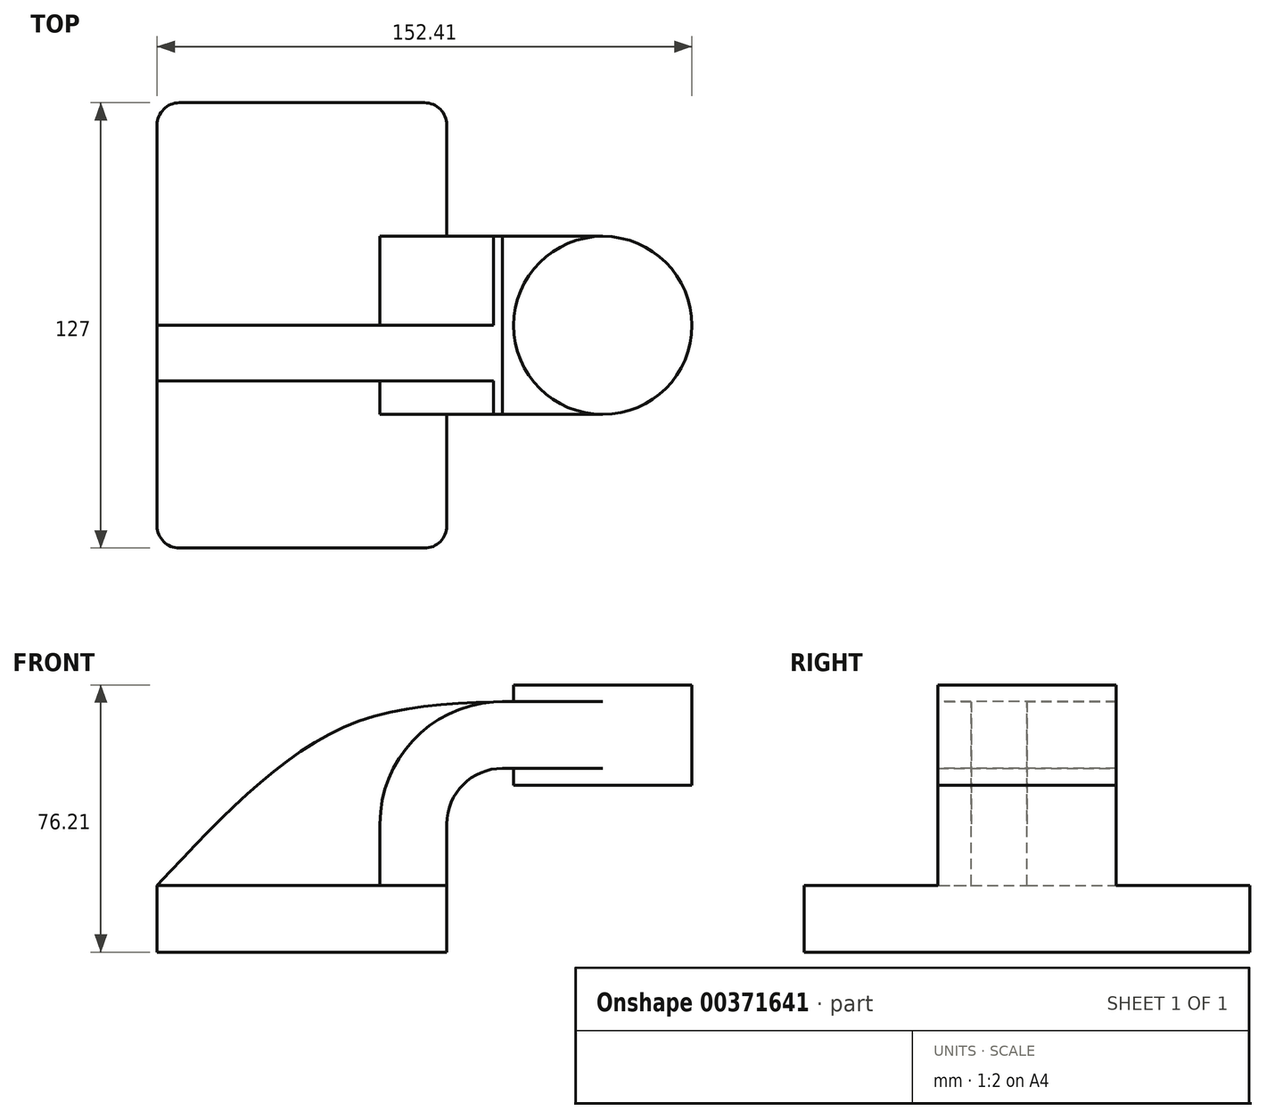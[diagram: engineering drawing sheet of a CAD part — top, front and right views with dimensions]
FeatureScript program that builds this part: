
annotation { "Feature Type Name" : "Feature", "Feature Type Description" : "" }
export const myFeature = defineFeature(function(context is Context, id is Id, definition is map)
    precondition{}
    {
        {
            var Q0;
            Q0=qCreatedBy(makeId("Front.planeOp"),FACE);
            var sketch = newSketch(context, id + "F0", { "sketchPlane" : qUnion([Q0])});
            skLineSegment(sketch, "E0.bottom", {"start": v(41.28, 9.52) * mm, "end": v(-41.28, 9.52) * mm});
            skLineSegment(sketch, "E0.top", {"start": v(41.28, -9.53) * mm, "end": v(-41.28, -9.53) * mm});
            skLineSegment(sketch, "E0.left", {"start": v(41.28, 9.53) * mm, "end": v(41.28, -9.53) * mm});
            skLineSegment(sketch, "E0.right", {"start": v(-41.28, 9.52) * mm, "end": v(-41.27, -9.53) * mm});
            skPoint(sketch, "E0.middle", {"position": v(0, 0) * mm});
            skLineSegment(sketch, "E1", {"start": v(41.28, 9.52) * mm, "end": v(41.28, 27) * mm});
            skArc(sketch, "E2", {"start": v(41.27, 27) * mm, "mid": v(45.92, 38.23) * mm, "end": v(57.15, 42.88) * mm});
            skLineSegment(sketch, "E3", {"start": v(57.15, 42.88) * mm, "end": v(85.73, 42.88) * mm});
            skLineSegment(sketch, "E4.bottom", {"start": v(60.33, 66.68) * mm, "end": v(111.13, 66.68) * mm});
            skLineSegment(sketch, "E4.top", {"start": v(60.33, 38.1) * mm, "end": v(111.13, 38.1) * mm});
            skLineSegment(sketch, "E4.left", {"start": v(60.33, 66.68) * mm, "end": v(60.33, 38.1) * mm});
            skLineSegment(sketch, "E4.right", {"start": v(111.13, 66.68) * mm, "end": v(111.13, 38.1) * mm});
            skPoint(sketch, "E4.middle", {"position": v(85.73, 52.39) * mm});
            skLineSegment(sketch, "E5.0", {"start": v(57.15, 61.93) * mm, "end": v(85.73, 61.93) * mm});
            skArc(sketch, "E5.1", {"start": v(22.23, 27) * mm, "mid": v(32.45, 51.7) * mm, "end": v(57.15, 61.93) * mm});
            skLineSegment(sketch, "E5.2", {"start": v(22.23, 9.52) * mm, "end": v(22.23, 27) * mm});
            skPoint(sketch, "E6.startSnap0", {"position": v(85.73, 66.68) * mm});
            skFitSpline(sketch, "E7", {"points": [v(-41.28, 9.52) * mm, v(-10.95, 39.6) * mm, v(19.24, 57.36) * mm, v(57.15, 61.93) * mm], "startDerivative": vector(85.37, 91.2) * mm, "endDerivative": vector(119, 4.27) * mm});
            skLineSegment(sketch, "E8", {"start": v(85.73, 66.68) * mm, "end": v(85.73, 38.1) * mm});
            skSolve(sketch);
        }
        {
            var Q0;
            Q0=makeQuery(id+"F0.imprint","IMPRINT",FACE,{"disambiguationData":[TD([[makeQuery(id+"F0.imprint","IMPRINT",EDGE,{"derivedFrom":sQuery(id+"F0.wireOp",EDGE,"E0.top")}),-1.0]])]});
            extrude(context, id + "F1", {"entities" : qUnion([Q0]), "endBound" : BoundingType.SYMMETRIC, "depth" : 127 * mm});
        }
        {
            var Q0;
            {var subQ8=sQuery(id+"F0.wireOp",EDGE,"E1");Q0=makeQuery(id+"F0.imprint","IMPRINT",FACE,{"disambiguationData":[TD([[makeQuery(id+"F0.imprint","IMPRINT",EDGE,{"derivedFrom":subQ8}),1.0]])]});}
            var Q1;
            {var subQ0=sQuery(id+"F0.wireOp",EDGE,"RDqRDKUh-tZSh-ccH2-2HAj-dexB6HYa6Owt");Q1=makeQuery(id+"F0.imprint","IMPRINT",FACE,{"disambiguationData":[TD([[makeQuery(id+"F0.imprint","IMPRINT",EDGE,{"derivedFrom":subQ0}),-1.0]])]});}
            var Q2;
            {var subQ0=sQuery(id+"F0.wireOp",EDGE,"E8");var subQ1=sQuery(id+"F0.wireOp",EDGE,"E3");var subQ2=makeQuery(id+"F0.imprint","INTERSECT",VERTEX,{"derivedFrom":[subQ1,subQ0]});Q2=makeQuery(id+"F0.imprint","IMPRINT",FACE,{"disambiguationData":[TD([[makeQuery(id+"F0.imprint","IMPRINT",EDGE,{"disambiguationData":[TD([[subQ2,1.0]])],"derivedFrom":subQ1}),1.0]])]});}
            extrude(context, id + "F2", {"entities" : qUnion([Q0, Q1, Q2]), "operationType" : NewBodyOperationType.ADD, "endBound" : BoundingType.SYMMETRIC, "depth" : 50.8 * mm});
        }
        {
            var Q0;
            {var subQ3=sQuery(id+"F0.wireOp",EDGE,"E5.2");Q0=makeQuery(id+"F0.imprint","IMPRINT",FACE,{"disambiguationData":[TD([[makeQuery(id+"F0.imprint","IMPRINT",EDGE,{"derivedFrom":subQ3}),1.0]])]});}
            extrude(context, id + "F3", {"entities" : qUnion([Q0]), "operationType" : NewBodyOperationType.ADD, "depth" : 15.88 * mm});
        }
        {
            var Q0;
            {var subQ4=sQuery(id+"F0.wireOp",EDGE,"E4.right");Q0=makeQuery(id+"F0.imprint","IMPRINT",FACE,{"disambiguationData":[TD([[makeQuery(id+"F0.imprint","IMPRINT",EDGE,{"derivedFrom":subQ4}),-1.0]])]});}
            var Q1;
            Q1=sQuery(id+"F0.wireOp",EDGE,"E8");
            revolve(context, id + "F4", {"operationType" : NewBodyOperationType.ADD, "entities" : qUnion([Q0]), "axis" : qUnion([Q1]), "revolveType" : RevolveType.FULL});
        }
        {
            var Q0;
            Q0=makeQuery(id+"F1.opExtrude","CAP_EDGE",EDGE,{"disambiguationData":[OSD([sQuery(id+"F0.wireOp",EDGE,"E0.right")])],"isStart":false});
            var Q1;
            Q1=makeQuery(id+"F1.opExtrude","CAP_EDGE",EDGE,{"disambiguationData":[OSD([sQuery(id+"F0.wireOp",EDGE,"E0.right")])],"isStart":true});
            var Q2;
            Q2=makeQuery(id+"F1.opExtrude","CAP_EDGE",EDGE,{"disambiguationData":[OSD([sQuery(id+"F0.wireOp",EDGE,"E0.left")])],"isStart":true});
            var Q3;
            Q3=makeQuery(id+"F1.opExtrude","CAP_EDGE",EDGE,{"disambiguationData":[OSD([sQuery(id+"F0.wireOp",EDGE,"E0.left")])],"isStart":false});
            fillet(context, id + "F5", {"entities" : qUnion([Q0, Q1, Q2, Q3]), "radius" : 6.35 * mm, "tangentPropagation" : true, "allowEdgeOverflow" : false});
        }
    });
